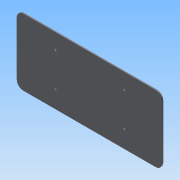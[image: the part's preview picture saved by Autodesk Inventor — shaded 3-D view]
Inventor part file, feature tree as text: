
AUTODESK INVENTOR PART (.ipt)
format: ipt  version: 2014 (Build 180170000, 170)  size: 96,768 bytes
history: native  units: in
note: dims shown in document units (in); Inventor stores cm internally (conversion verified against a paired STEP export)
features: extrude x2, sketch x2, fillet x1
ambient origin geometry x8: Origin, YZ Plane, XZ Plane, XY Plane, X Axis, Y Axis, Z Axis, Center Point
bodies: Solid1 (feature_tree)
feature tree (5):
  extrude  "Extrusion1"  Depth=8.5in
  fillet  "Fillet1"  Radius=0.07in
  extrude  "Extrusion2"  Depth=0.375in
  sketch  "Sketch1"  dims[d0=3.9in d1=8.5in d2=0.07in d3=0.0in]
  sketch  "Sketch2"  dims[d4=0.375in d5=2.226in d6=0.91in d7=1.01in d8=2.25in d9=0.125in d10=1.0in d11=0.0in]
